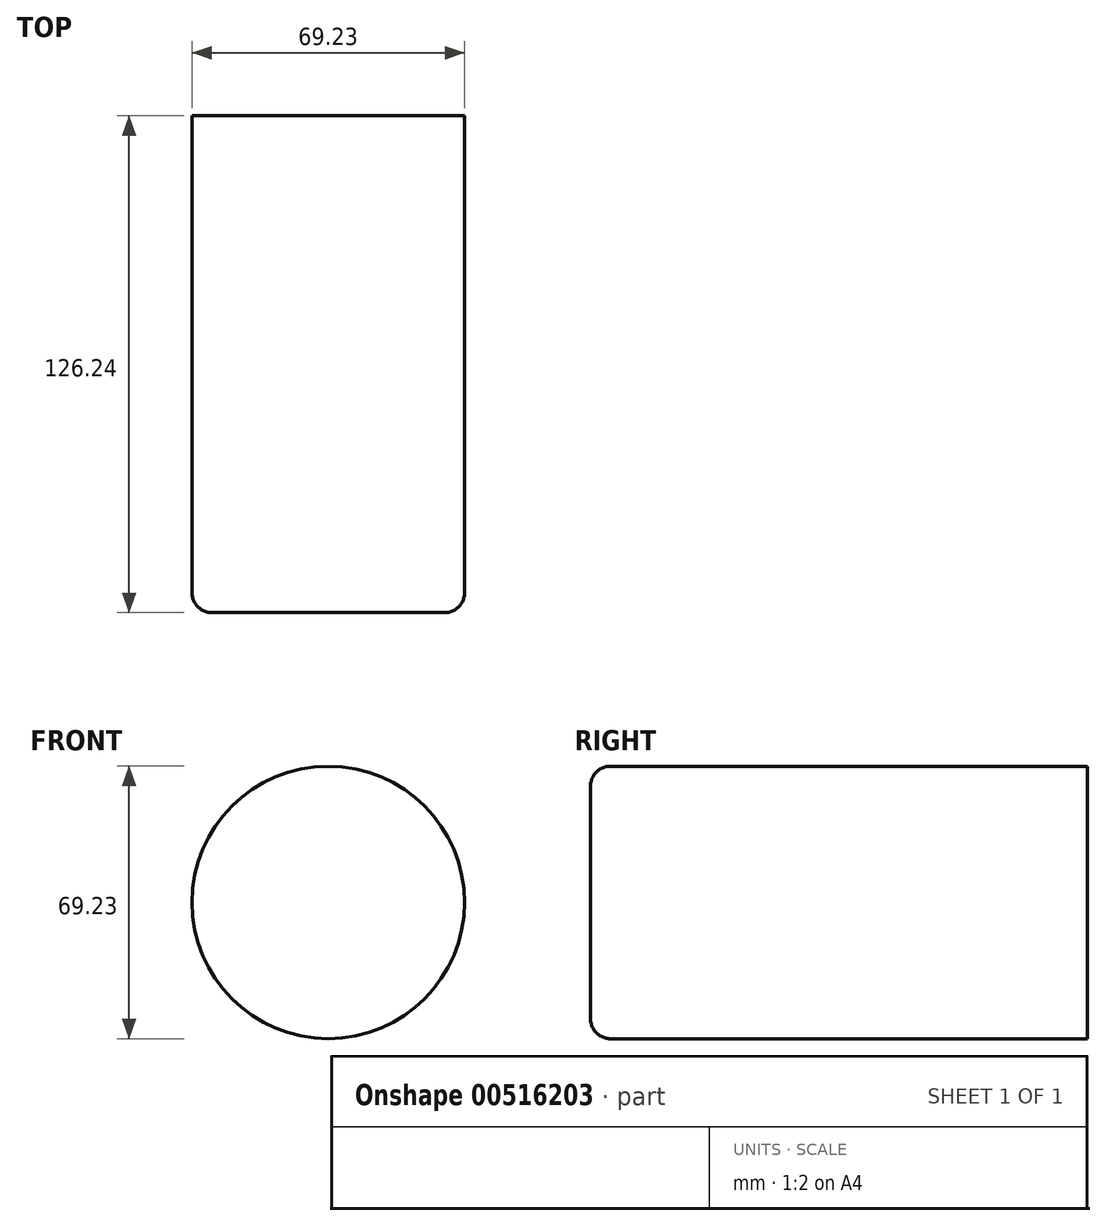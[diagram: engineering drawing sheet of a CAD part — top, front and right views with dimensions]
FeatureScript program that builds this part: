
annotation { "Feature Type Name" : "Feature", "Feature Type Description" : "" }
export const myFeature = defineFeature(function(context is Context, id is Id, definition is map)
    precondition{}
    {
        {
            var Q0;
            Q0=qCreatedBy(makeId("Front.planeOp"),FACE);
            var sketch = newSketch(context, id + "F0", { "sketchPlane" : qUnion([Q0])});
            skCircle(sketch, "E0", {"center": v(-68.2, 29.23) * mm, "radius": 34.62 * mm});
            skSolve(sketch);
        }
        {
            var Q0;
            Q0=makeQuery(id+"F0.imprint","IMPRINT",FACE,{"disambiguationData":[TD([[makeQuery(id+"F0.imprint","IMPRINT",EDGE,{"derivedFrom":sQuery(id+"F0.wireOp",EDGE,"E0")}),1.0]])]});
            extrude(context, id + "F1", {"entities" : qUnion([Q0]), "depth" : 126.24 * mm, "offsetDistance" : 25.4 * mm});
        }
        {
            var Q0;
            Q0=makeQuery(id+"F1.opExtrude","CAP_EDGE",EDGE,{"disambiguationData":[OSD([sQuery(id+"F0.wireOp",EDGE,"E0")])],"isStart":false});
            fillet(context, id + "F2", {"entities" : qUnion([Q0]), "radius" : 5.08 * mm, "tangentPropagation" : true, "allowEdgeOverflow" : false});
        }
    });
